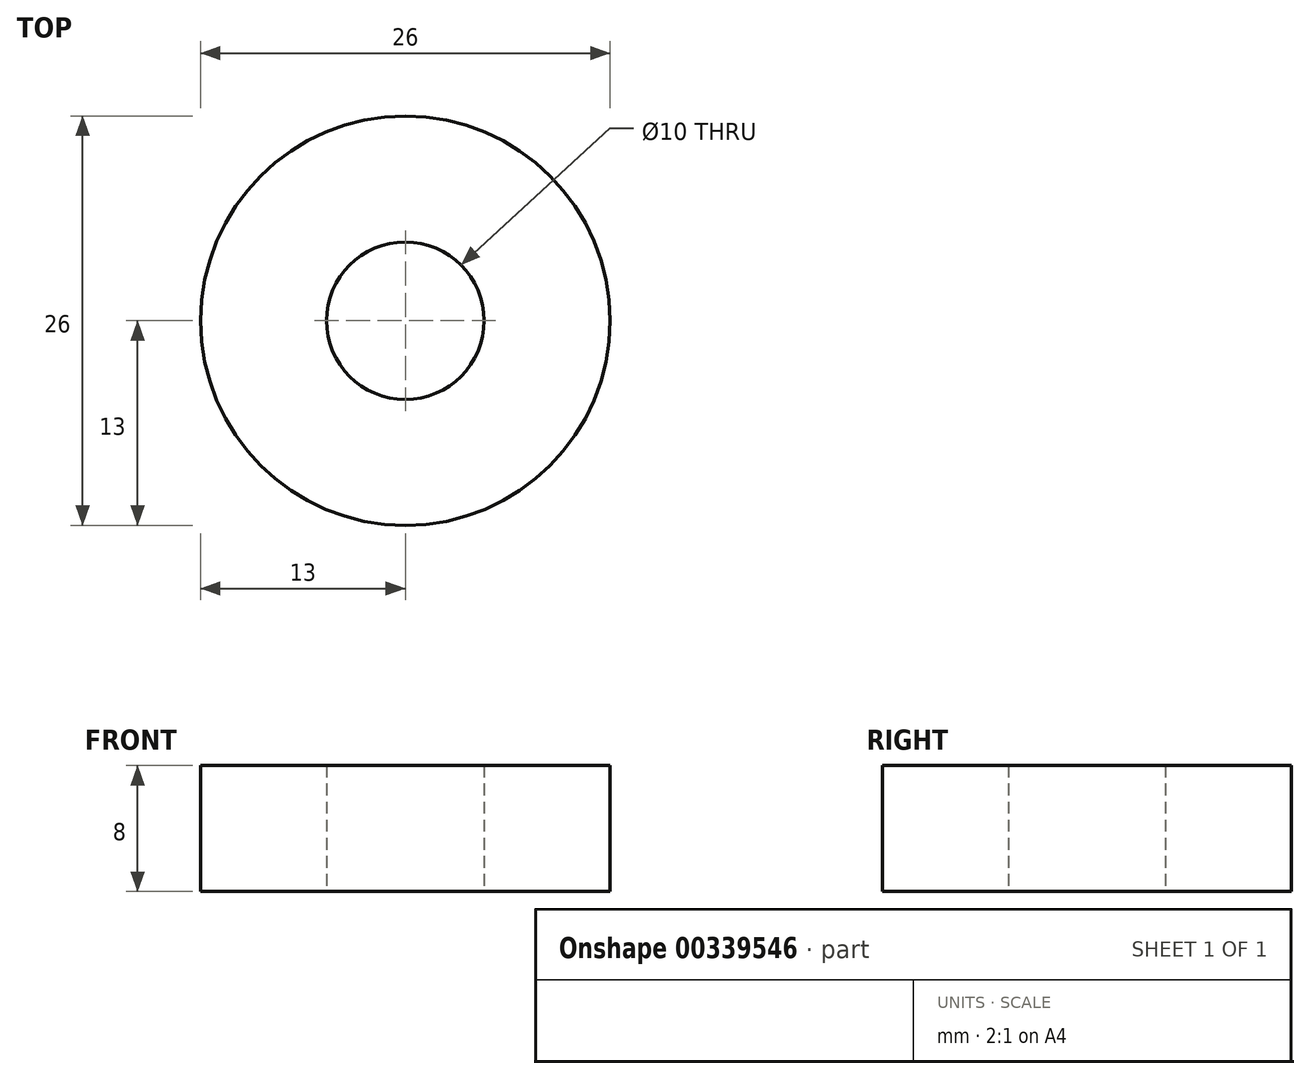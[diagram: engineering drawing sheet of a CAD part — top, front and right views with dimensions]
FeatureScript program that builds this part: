
annotation { "Feature Type Name" : "Feature", "Feature Type Description" : "" }
export const myFeature = defineFeature(function(context is Context, id is Id, definition is map)
    precondition{}
    {
        {
            var Q0;
            Q0=qCreatedBy(makeId("Top.planeOp"),FACE);
            var sketch = newSketch(context, id + "F0", { "sketchPlane" : qUnion([Q0])});
            skCircle(sketch, "E0", {"center": v(0, 0) * mm, "radius": 5 * mm});
            skCircle(sketch, "E1", {"center": v(0, 0) * mm, "radius": 13 * mm});
            skSolve(sketch);
        }
        {
            var Q0;
            Q0 = qSketchRegion(id + "F0", true);
            extrude(context, id + "F1", {"entities" : qUnion([Q0]), "depth" : 8 * mm});
        }
    });
